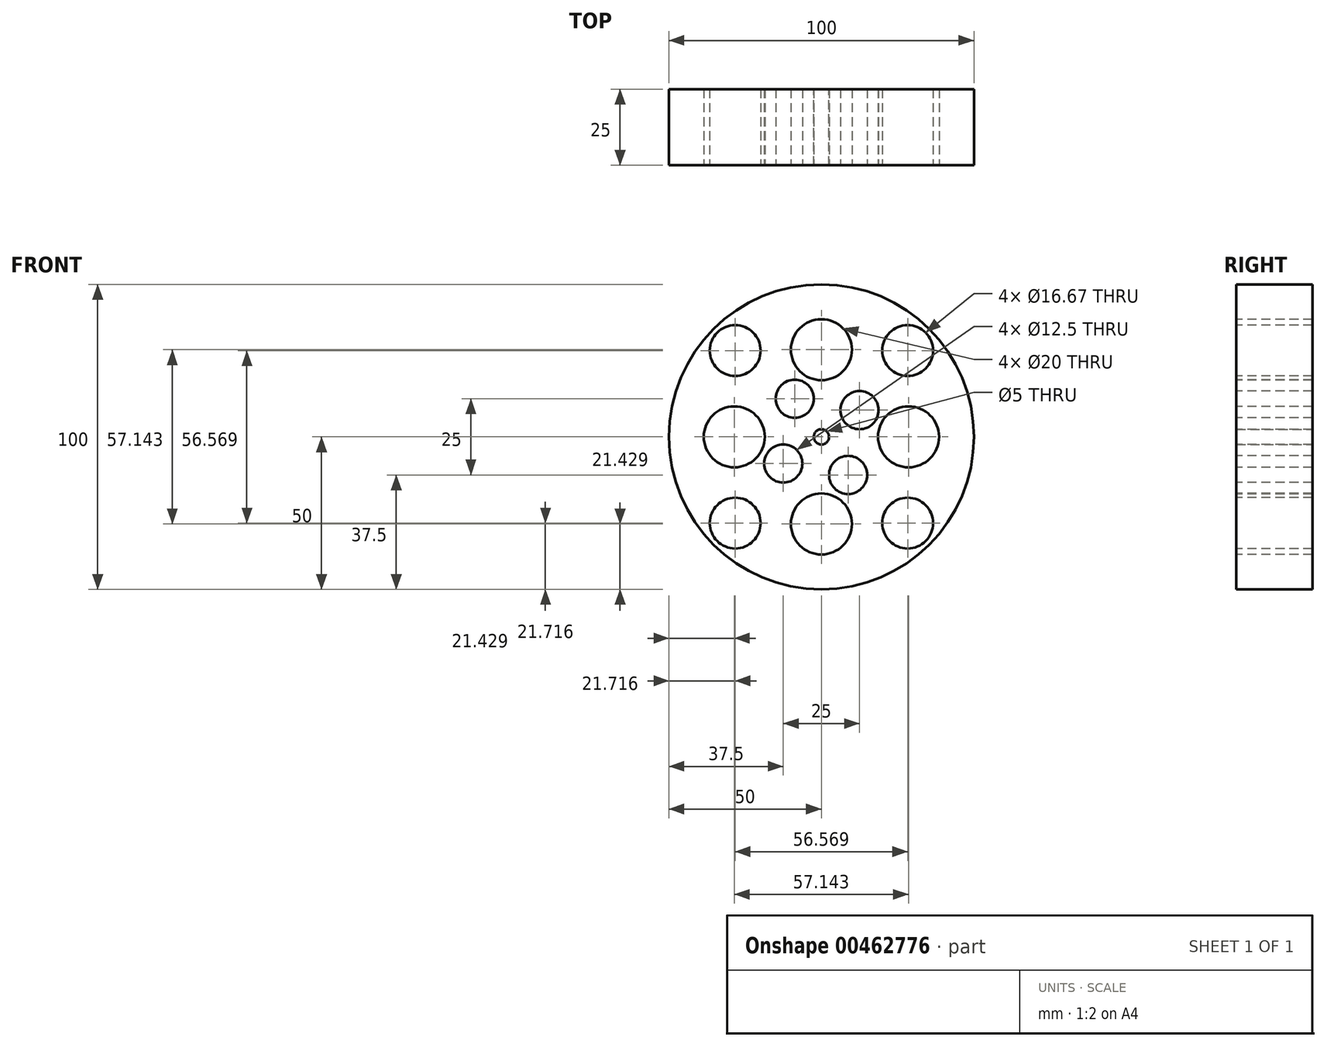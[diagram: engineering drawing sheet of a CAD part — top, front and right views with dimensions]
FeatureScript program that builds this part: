
annotation { "Feature Type Name" : "Feature", "Feature Type Description" : "" }
export const myFeature = defineFeature(function(context is Context, id is Id, definition is map)
    precondition{}
    {
        {
            var Q0;
            Q0=qCreatedBy(makeId("Front.planeOp"),FACE);
            var sketch = newSketch(context, id + "F0", { "sketchPlane" : qUnion([Q0])});
            skCircle(sketch, "E0", {"center": v(0, 0) * mm, "radius": 50 * mm});
            skCircle(sketch, "E1", {"center": v(0, 0) * mm, "radius": 2.5 * mm});
            skSolve(sketch);
        }
        {
            var Q0;
            Q0=qSketchRegion(id+"F0",true);
            extrude(context, id + "F1", {"entities" : qUnion([Q0]), "depth" : 25 * mm});
        }
        {
            var Q0;
            Q0=makeQuery(id+"F1.opExtrude","CAP_FACE",FACE,{"disambiguationData":[OSD([sQuery(id+"F0.wireOp",EDGE,"E0"),sQuery(id+"F0.wireOp",EDGE,"E1")])],"isStart":false});
            var sketch = newSketch(context, id + "F2", { "sketchPlane" : qUnion([Q0])});
            skLineSegment(sketch, "E2", {"start": v(0, 0) * mm, "end": v(0, 352.88) * mm, "construction": true});
            skLineSegment(sketch, "E3", {"start": v(0, 0) * mm, "end": v(224.42, 0) * mm, "construction": true});
            skCircle(sketch, "E4", {"center": v(0, 28.57) * mm, "radius": 10 * mm});
            skLineSegment(sketch, "E5", {"start": v(0, 0) * mm, "end": v(189.63, 189.63) * mm, "construction": true});
            skCircle(sketch, "E6", {"center": v(28.28, 28.28) * mm, "radius": 8.33 * mm});
            skLineSegment(sketch, "E7", {"start": v(0, 0) * mm, "end": v(126.37, 88.48) * mm, "construction": true});
            skCircle(sketch, "E8", {"center": v(12.5, 8.75) * mm, "radius": 6.25 * mm});
            skCircle(sketch, "E9.1.0", {"center": v(-28.57, 0) * mm, "radius": 10 * mm});
            skCircle(sketch, "E9.1.1", {"center": v(-28.28, 28.28) * mm, "radius": 8.33 * mm});
            skCircle(sketch, "E9.1.2", {"center": v(-8.75, 12.5) * mm, "radius": 6.25 * mm});
            skCircle(sketch, "E9.2.0", {"center": v(0, -28.57) * mm, "radius": 10 * mm});
            skCircle(sketch, "E9.2.1", {"center": v(-28.28, -28.28) * mm, "radius": 8.33 * mm});
            skCircle(sketch, "E9.2.2", {"center": v(-12.5, -8.75) * mm, "radius": 6.25 * mm});
            skCircle(sketch, "E9.3.0", {"center": v(28.57, 0) * mm, "radius": 10 * mm});
            skCircle(sketch, "E9.3.1", {"center": v(28.28, -28.28) * mm, "radius": 8.33 * mm});
            skCircle(sketch, "E9.3.2", {"center": v(8.75, -12.5) * mm, "radius": 6.25 * mm});
            skPoint(sketch, "E9.center", {"position": v(0, 0) * mm});
            skSolve(sketch);
        }
        {
            var Q0;
            Q0=makeQuery(id+"F2.imprint","IMPRINT",FACE,{"disambiguationData":[TD([[makeQuery(id+"F2.imprint","IMPRINT",EDGE,{"derivedFrom":sQuery(id+"F2.wireOp",EDGE,"E9.1.1")}),1.0]])]});
            var Q1;
            Q1=makeQuery(id+"F2.imprint","IMPRINT",FACE,{"disambiguationData":[TD([[makeQuery(id+"F2.imprint","IMPRINT",EDGE,{"derivedFrom":sQuery(id+"F2.wireOp",EDGE,"E4")}),1.0]])]});
            var Q2;
            Q2=makeQuery(id+"F2.imprint","IMPRINT",FACE,{"disambiguationData":[TD([[makeQuery(id+"F2.imprint","IMPRINT",EDGE,{"derivedFrom":sQuery(id+"F2.wireOp",EDGE,"E9.1.2")}),1.0]])]});
            var Q3;
            Q3=makeQuery(id+"F2.imprint","IMPRINT",FACE,{"disambiguationData":[TD([[makeQuery(id+"F2.imprint","IMPRINT",EDGE,{"derivedFrom":sQuery(id+"F2.wireOp",EDGE,"E8")}),1.0]])]});
            var Q4;
            Q4=makeQuery(id+"F2.imprint","IMPRINT",FACE,{"disambiguationData":[TD([[makeQuery(id+"F2.imprint","IMPRINT",EDGE,{"derivedFrom":sQuery(id+"F2.wireOp",EDGE,"E6")}),1.0]])]});
            var Q5;
            Q5=makeQuery(id+"F2.imprint","IMPRINT",FACE,{"disambiguationData":[TD([[makeQuery(id+"F2.imprint","IMPRINT",EDGE,{"derivedFrom":sQuery(id+"F2.wireOp",EDGE,"E9.3.0")}),1.0]])]});
            var Q6;
            Q6=makeQuery(id+"F2.imprint","IMPRINT",FACE,{"disambiguationData":[TD([[makeQuery(id+"F2.imprint","IMPRINT",EDGE,{"derivedFrom":sQuery(id+"F2.wireOp",EDGE,"E9.1.0")}),1.0]])]});
            var Q7;
            Q7=makeQuery(id+"F2.imprint","IMPRINT",FACE,{"disambiguationData":[TD([[makeQuery(id+"F2.imprint","IMPRINT",EDGE,{"derivedFrom":sQuery(id+"F2.wireOp",EDGE,"E9.2.1")}),1.0]])]});
            var Q8;
            Q8=makeQuery(id+"F2.imprint","IMPRINT",FACE,{"disambiguationData":[TD([[makeQuery(id+"F2.imprint","IMPRINT",EDGE,{"derivedFrom":sQuery(id+"F2.wireOp",EDGE,"E9.2.0")}),1.0]])]});
            var Q9;
            Q9=makeQuery(id+"F2.imprint","IMPRINT",FACE,{"disambiguationData":[TD([[makeQuery(id+"F2.imprint","IMPRINT",EDGE,{"derivedFrom":sQuery(id+"F2.wireOp",EDGE,"E9.2.2")}),1.0]])]});
            var Q10;
            Q10=makeQuery(id+"F2.imprint","IMPRINT",FACE,{"disambiguationData":[TD([[makeQuery(id+"F2.imprint","IMPRINT",EDGE,{"derivedFrom":sQuery(id+"F2.wireOp",EDGE,"E9.3.1")}),1.0]])]});
            var Q11;
            Q11=makeQuery(id+"F2.imprint","IMPRINT",FACE,{"disambiguationData":[TD([[makeQuery(id+"F2.imprint","IMPRINT",EDGE,{"derivedFrom":sQuery(id+"F2.wireOp",EDGE,"E9.3.2")}),1.0]])]});
            extrude(context, id + "F3", {"entities" : qUnion([Q0, Q1, Q2, Q3, Q4, Q5, Q6, Q7, Q8, Q9, Q10, Q11]), "operationType" : NewBodyOperationType.REMOVE, "oppositeDirection" : true, "depth" : 25 * mm});
        }
    });
